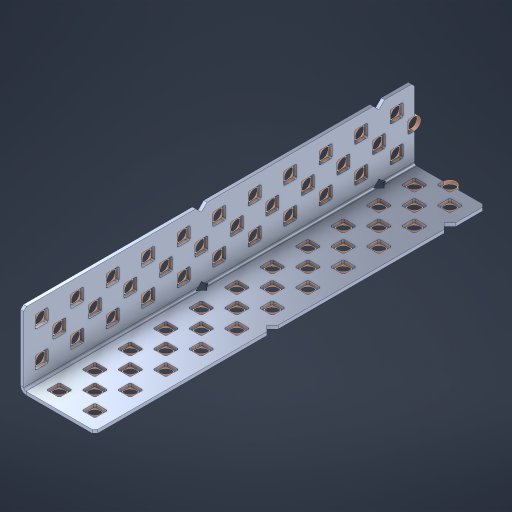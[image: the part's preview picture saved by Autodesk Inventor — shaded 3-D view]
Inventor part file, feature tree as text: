
AUTODESK INVENTOR PART (.ipt)
format: ipt  version: 2023 (Build 270158000, 158)  size: 1,041,408 bytes
history: native  units: in
note: dims shown in document units (in); Inventor stores cm internally (conversion verified against a paired STEP export)
features: other x72, extrude x64, sheet_metal_op x8, sketch x7, pattern_linear x2, mirror x1, chamfer x1
ambient origin geometry x8: Origin, YZ Plane, XZ Plane, XY Plane, X Axis, Y Axis, Z Axis, Center Point
bodies: Solid1 (feature_tree), Body (feature_tree)
feature tree (155):
  sheet_metal_op  "Flanges"
  sheet_metal_op  "Body Pattern"
  pattern_linear  "Center Pattern"  Spacing1=1.0in  [1 undecoded]
  other  "Arc Length"
  pattern_linear  "Notch Pattern"  Spacing1=0.1875in  [1 undecoded]
  other  "Diagonal Plane"
  mirror  "Everything Mirrored"
  chamfer  "End Chamfer"
  sketch  "Sketch1"  dims[d0=1.0in]
  other  "Plate1"
  sketch  "Sketch2"  dims[d1=5.5in]
  other  "Plate2"
  sheet_metal_op  "Bend1"
  sheet_metal_op  "Corner1"
  sketch  "Sketch8"  dims[d2=0.0469in]
  sketch  "Sketch9"  dims[d3=0.0469in]
  other  "Srf91"
  sheet_metal_op  "Body Pattern Sketch"
  other  "Srf92"
  sketch  "Sketch13"  dims[d4=0.0234in]
  sketch  "Sketch15"  dims[d5=0.0938in]
  sketch  "Sketch16"  dims[d6=0.0469in d7=1.0in d8=90.0deg d9=0.0312in d10=0.1875in d11=0.0469in d12=0.0469in d49=0.182in d50=0.02in d52=0.25in d53=0.0469in d54=0.0in d55=0.172in d56=1.0in d57=0.0in d60=4.3307in d62=0.5in d63=0.7874in d65=0.5in d85=0.1473in d86=0.1659in d89=0.0469in d90=0.0in d91=0.04in d92=0.0491in d95=2.5in d96=0.04in d97=0.25in d98=45.0deg d99=0.25in d106=0.182in d107=0.02in d108=0.5in d110=0.0469in d111=0.0in d112=0.172in d113=0.5in d114=0.0in d117=0.5in d123=0.25in d125=0.25in d126=0.0491in d127=0.1227in d128=0.08in d129=0.04in d130=2.5in]
  other  "Srf786"
  other  "Srf856"
  other  "Srf857"
  other  "Srf858"
  other  "Srf859"
  other  "Srf860"
  other  "Srf861"
  other  "Srf889"
  other  "Srf890"
  other  "Srf891"
  other  "Srf1275"
  other  "Srf1276"
  other  "Srf1278"
  other  "Srf1279"
  other  "Srf1280"
  other  "Srf1281"
  other  "Srf1282"
  other  "Srf1283"
  other  "Srf1277"
  other  "Srf1285"
  other  "Srf1286"
  other  "Srf1287"
  other  "Srf1383"
  other  "Srf1384"
  other  "Srf1385"
  other  "Srf1386"
  other  "Srf1387"
  other  "Srf1388"
  other  "Srf1389"
  other  "Srf1390"
  other  "Srf1391"
  other  "Srf1392"
  other  "Srf1393"
  other  "Srf1394"
  other  "Srf1395"
  other  "Srf1396"
  other  "Srf1445"
  other  "Srf1446"
  other  "Srf1447"
  other  "Srf1448"
  other  "Srf1449"
  other  "Srf1450"
  other  "Srf1451"
  other  "Srf1475"
  other  "Srf1476"
  other  "Srf1477"
  other  "Srf1478"
  other  "Srf1479"
  other  "Srf1480"
  other  "Srf1481"
  other  "Srf1482"
  other  "Srf1483"
  other  "Srf1484"
  other  "Srf1485"
  other  "Srf1486"
  other  "Srf1487"
  other  "Srf1488"
  other  "Srf1537"
  other  "Srf1538"
  other  "Srf1539"
  other  "Srf1540"
  other  "Srf1541"
  other  "Srf1542"
  other  "Srf1543"
  sheet_metal_op  "Body Stamp"
  sheet_metal_op  "Body Circle"
  other  "Center Stamp"
  other  "Center Circle"
  sheet_metal_op  "Notch"
  extrude  "ExtrusionSrf92"  Depth=0.0469in
  extrude  "ExtrusionSrf856"  Depth=0.0469in
  extrude  "ExtrusionSrf857"  Depth=0.182in
  extrude  "ExtrusionSrf858"  Depth=0.02in
  extrude  "ExtrusionSrf859"  Depth=0.25in
  extrude  "ExtrusionSrf860"  Depth=0.0469in
  extrude  "ExtrusionSrf861"  TaperAngle=0.0deg  [1 undecoded]
  extrude  "ExtrusionSrf889"  Depth=2.5in
  extrude  "ExtrusionSrf890"  Depth=1.0in TaperAngle=0.0deg
  extrude  "ExtrusionSrf891"  Depth=2.5in
  extrude  "ExtrusionSrf1275"  Depth=0.5in
  extrude  "ExtrusionSrf1276"  Depth=2.5in
  extrude  "ExtrusionSrf1277"  Depth=2.5in
  extrude  "ExtrusionSrf1278"  Depth=0.0469in
  extrude  "ExtrusionSrf1279"  Depth=2.5in TaperAngle=0.0deg
  extrude  "ExtrusionSrf1280"  Depth=2.5in
  extrude  "ExtrusionSrf1281"  Depth=0.25in TaperAngle=45.0deg
  extrude  "ExtrusionSrf1282"  Depth=0.25in
  extrude  "ExtrusionSrf1345"  Depth=0.182in
  extrude  "ExtrusionSrf1346"  Depth=0.02in
  extrude  "ExtrusionSrf1347"  Depth=0.5in
  extrude  "ExtrusionSrf1348"  Depth=0.0469in
  extrude  "ExtrusionSrf1383"  TaperAngle=0.0deg  [1 undecoded]
  extrude  "ExtrusionSrf1384"  Depth=2.5in
  extrude  "ExtrusionSrf1385"  Depth=0.5in TaperAngle=0.0deg
  extrude  "ExtrusionSrf1386"  Depth=0.5in
  extrude  "ExtrusionSrf1387"  Depth=0.25in
  extrude  "ExtrusionSrf1388"  Depth=0.25in
  extrude  "ExtrusionSrf1389"  Depth=2.5in
  extrude  "ExtrusionSrf1390"  Depth=2.5in
  extrude  "ExtrusionSrf1391"  Depth=2.5in
  extrude  "ExtrusionSrf1392"  Depth=2.5in
  extrude  "ExtrusionSrf1393"  Depth=2.5in
  extrude  "ExtrusionSrf1394"  [1 undecoded]
  extrude  "ExtrusionSrf1395"  [1 undecoded]
  extrude  "ExtrusionSrf1396"  [1 undecoded]
  extrude  "ExtrusionSrf1445"  [1 undecoded]
  extrude  "ExtrusionSrf1446"  [1 undecoded]
  extrude  "ExtrusionSrf1447"  [1 undecoded]
  extrude  "ExtrusionSrf1448"  [1 undecoded]
  extrude  "ExtrusionSrf1449"  [1 undecoded]
  extrude  "ExtrusionSrf1450"  [1 undecoded]
  extrude  "ExtrusionSrf1451"  [1 undecoded]
  extrude  "ExtrusionSrf1475"  [1 undecoded]
  extrude  "ExtrusionSrf1476"  [1 undecoded]
  extrude  "ExtrusionSrf1477"  [1 undecoded]
  extrude  "ExtrusionSrf1478"  [1 undecoded]
  extrude  "ExtrusionSrf1479"  [1 undecoded]
  extrude  "ExtrusionSrf1480"  [1 undecoded]
  extrude  "ExtrusionSrf1481"  [1 undecoded]
  extrude  "ExtrusionSrf1482"  [1 undecoded]
  extrude  "ExtrusionSrf1483"  [1 undecoded]
  extrude  "ExtrusionSrf1484"  [1 undecoded]
  extrude  "ExtrusionSrf1485"  [1 undecoded]
  extrude  "ExtrusionSrf1486"  [1 undecoded]
  extrude  "ExtrusionSrf1487"  [1 undecoded]
  extrude  "ExtrusionSrf1488"  [1 undecoded]
  extrude  "ExtrusionSrf1537"  [1 undecoded]
  extrude  "ExtrusionSrf1538"  [1 undecoded]
  extrude  "ExtrusionSrf1539"  [1 undecoded]
  extrude  "ExtrusionSrf1540"  [1 undecoded]
  extrude  "ExtrusionSrf1541"  [1 undecoded]
  extrude  "ExtrusionSrf1542"  [1 undecoded]
  extrude  "ExtrusionSrf1543"  [1 undecoded]
note: 35 required parameter values undecoded (feature->parameter linkage not recoverable at this tier; creation-order binding heuristic only, values carry confidence <= 0.55)
